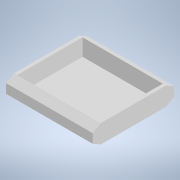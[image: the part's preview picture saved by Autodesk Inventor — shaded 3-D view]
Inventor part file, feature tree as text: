
AUTODESK INVENTOR PART (.ipt)
format: ipt  version: 2020 (Build 240168000, 168)  size: 120,320 bytes
history: native  units: in
note: dims shown in document units (in); Inventor stores cm internally (conversion verified against a paired STEP export)
features: extrude x2, sketch x2, projected_geometry x1
ambient origin geometry x8: Origin, YZ Plane, XZ Plane, XY Plane, X Axis, Y Axis, Z Axis, Center Point
bodies: Solid1 (feature_tree)
feature tree (5):
  extrude  "Extrusion1"  Depth=5.9055in
  extrude  "Extrusion2"  TaperAngle=0.0deg  [1 undecoded]
  sketch  "Sketch1"  dims[d0=1.3386in d1=5.9055in]
  sketch  "Sketch2"  dims[d2=6.2992in d3=0.0in d4=0.2362in d5=1.2205in d6=0.0in]
  projected_geometry  "Projected Loop1"
note: 1 required parameter value undecoded (feature->parameter linkage not recoverable at this tier; creation-order binding heuristic only, values carry confidence <= 0.55)
